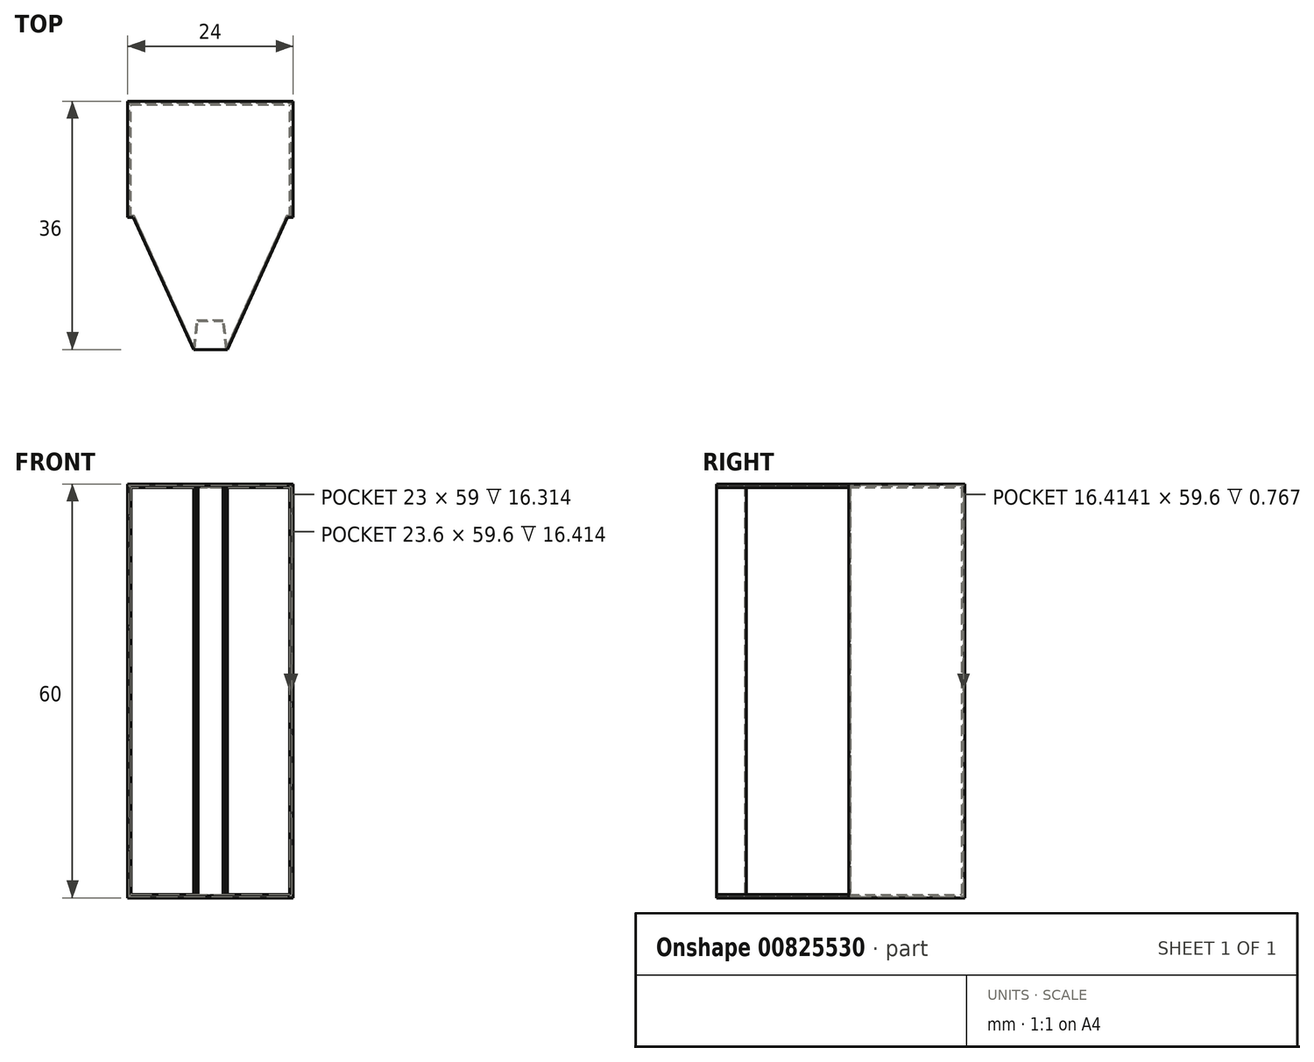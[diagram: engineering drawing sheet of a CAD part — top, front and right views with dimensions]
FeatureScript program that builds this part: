
annotation { "Feature Type Name" : "Feature", "Feature Type Description" : "" }
export const myFeature = defineFeature(function(context is Context, id is Id, definition is map)
    precondition{}
    {
        {
            var Q0;
            Q0=qCreatedBy(makeId("Front.planeOp"),FACE);
            var sketch = newSketch(context, id + "F0", { "sketchPlane" : qUnion([Q0])});
            skLineSegment(sketch, "E0.bottom", {"start": v(-14.2, 50.3) * mm, "end": v(9.8, 50.3) * mm});
            skLineSegment(sketch, "E0.top", {"start": v(-14.2, -9.7) * mm, "end": v(9.8, -9.7) * mm});
            skLineSegment(sketch, "E0.left", {"start": v(-14.2, 50.3) * mm, "end": v(-14.2, -9.7) * mm});
            skLineSegment(sketch, "E0.right", {"start": v(9.8, 50.3) * mm, "end": v(9.8, -9.7) * mm});
            skSolve(sketch);
        }
        {
            var Q0;
            Q0 = qSketchRegion(id + "F0", true);
            extrude(context, id + "F1", {"entities" : qUnion([Q0]), "depth" : 36 * mm, "offsetDistance" : 25 * mm});
        }
        {
            var Q0;
            Q0=makeQuery(id+"F1.opExtrude","SWEPT_FACE",FACE,{"disambiguationData":[OSD([sQuery(id+"F0.wireOp",EDGE,"E0.top")])]});
            var sketch = newSketch(context, id + "F2", { "sketchPlane" : qUnion([Q0])});
            skLineSegment(sketch, "E1", {"start": v(-13.37, 16.81) * mm, "end": v(-4.66, 36) * mm});
            skLineSegment(sketch, "E2", {"start": v(0.25, 36) * mm, "end": v(8.96, 16.81) * mm});
            skLineSegment(sketch, "E3", {"start": v(-14.2, 16.81) * mm, "end": v(-14.2, 36) * mm});
            skLineSegment(sketch, "E4", {"start": v(-14.2, 36) * mm, "end": v(-4.66, 36) * mm});
            skLineSegment(sketch, "E5", {"start": v(0.25, 36) * mm, "end": v(9.8, 36) * mm});
            skLineSegment(sketch, "E6", {"start": v(9.8, 36) * mm, "end": v(9.8, 16.81) * mm});
            skLineSegment(sketch, "E7", {"start": v(8.96, 16.81) * mm, "end": v(9.8, 16.81) * mm});
            skLineSegment(sketch, "E8", {"start": v(-14.2, 16.81) * mm, "end": v(-13.37, 16.81) * mm});
            skPoint(sketch, "E9.end.orphan", {"position": v(-13.37, 14.97) * mm});
            skPoint(sketch, "E10.orphan", {"position": v(-14.2, 14.97) * mm});
            skPoint(sketch, "E11.start.orphan", {"position": v(9.8, 14.97) * mm});
            skSolve(sketch);
        }
        {
            var Q0;
            Q0=makeQuery(id+"F1.opExtrude","CAP_FACE",FACE,{"disambiguationData":[OSD([sQuery(id+"F0.wireOp",EDGE,"E0.bottom"),sQuery(id+"F0.wireOp",EDGE,"E0.top"),sQuery(id+"F0.wireOp",EDGE,"E0.left"),sQuery(id+"F0.wireOp",EDGE,"E0.right")])],"isStart":false});
            shell(context, id + "F3", {"entities" : qUnion([Q0]), "thickness" : 0.5 * mm});
        }
        {
            var Q0;
            Q0=makeQuery(id+"F2.imprint","IMPRINT",FACE,{"disambiguationData":[TD([[makeQuery(id+"F2.imprint","IMPRINT",EDGE,{"derivedFrom":sQuery(id+"F2.wireOp",EDGE,"E1")}),1.0]])]});
            var Q1;
            Q1=makeQuery(id+"F2.imprint","IMPRINT",FACE,{"disambiguationData":[TD([[makeQuery(id+"F2.imprint","IMPRINT",EDGE,{"derivedFrom":sQuery(id+"F2.wireOp",EDGE,"E2")}),1.0]])]});
            extrude(context, id + "F4", {"entities" : qUnion([Q0, Q1]), "operationType" : NewBodyOperationType.REMOVE, "oppositeDirection" : true, "depth" : 197.7 * mm, "offsetDistance" : 25 * mm});
        }
        {
            var Q0;
            Q0=makeQuery(id+"F3.opShell","OFFSET_FACE",FACE,{"disambiguationData":[OSD([sQuery(id+"F0.wireOp",EDGE,"E0.top")])]});
            var sketch = newSketch(context, id + "F5", { "sketchPlane" : qUnion([Q0])});
            skLineSegment(sketch, "E12", {"start": v(-4.66, -36) * mm, "end": v(-4.19, -31.72) * mm});
            skLineSegment(sketch, "E13", {"start": v(0.25, -36) * mm, "end": v(-0.22, -31.72) * mm});
            skLineSegment(sketch, "E14", {"start": v(-4.19, -31.72) * mm, "end": v(-0.22, -31.72) * mm});
            skLineSegment(sketch, "E15", {"start": v(-4.66, -36) * mm, "end": v(0.25, -36) * mm});
            skSolve(sketch);
        }
        {
            var Q0;
            Q0 = qSketchRegion(id + "F5", true);
            var Q1;
            Q1=makeQuery(id+"F3.opShell","OFFSET_FACE",FACE,{"disambiguationData":[OSD([sQuery(id+"F0.wireOp",EDGE,"E0.bottom")])]});
            extrude(context, id + "F6", {"entities" : qUnion([Q0]), "operationType" : NewBodyOperationType.ADD, "endBound" : BoundingType.UP_TO_SURFACE, "depth" : 25 * mm, "endBoundEntityFace" : qUnion([Q1]), "offsetDistance" : 25 * mm});
        }
        {
            var Q0;
            {var subQ0=sQuery(id+"F0.wireOp",EDGE,"E0.top");var subQ3=sQuery(id+"F0.wireOp",EDGE,"E0.bottom");var subQ4=makeQuery(id+"F1.opExtrude","CAP_FACE",FACE,{"disambiguationData":[OSD([subQ3,subQ0,sQuery(id+"F0.wireOp",EDGE,"E0.left"),sQuery(id+"F0.wireOp",EDGE,"E0.right")])],"isStart":false});Q0=makeQuery(id+"F6.boolean.opBoolean","MERGE",FACE,{"derivedFrom":[makeQuery(id+"F4.boolean.opBoolean","SPLIT",FACE,{"disambiguationData":[TD([makeQuery(id+"F1.opExtrude","SWEPT_FACE",FACE,{"disambiguationData":[OSD([subQ3])]})])],"derivedFrom":subQ4}),makeQuery(id+"F4.boolean.opBoolean","SPLIT",FACE,{"disambiguationData":[TD([makeQuery(id+"F1.opExtrude","SWEPT_FACE",FACE,{"disambiguationData":[OSD([subQ0])]})])],"derivedFrom":subQ4}),makeQuery(id+"F6.opExtrude","SWEPT_FACE",FACE,{"disambiguationData":[OSD([sQuery(id+"F5.wireOp",EDGE,"E15")])]})]});}
            shell(context, id + "F7", {"entities" : qUnion([Q0]), "thickness" : 0.2 * mm});
        }
    });
